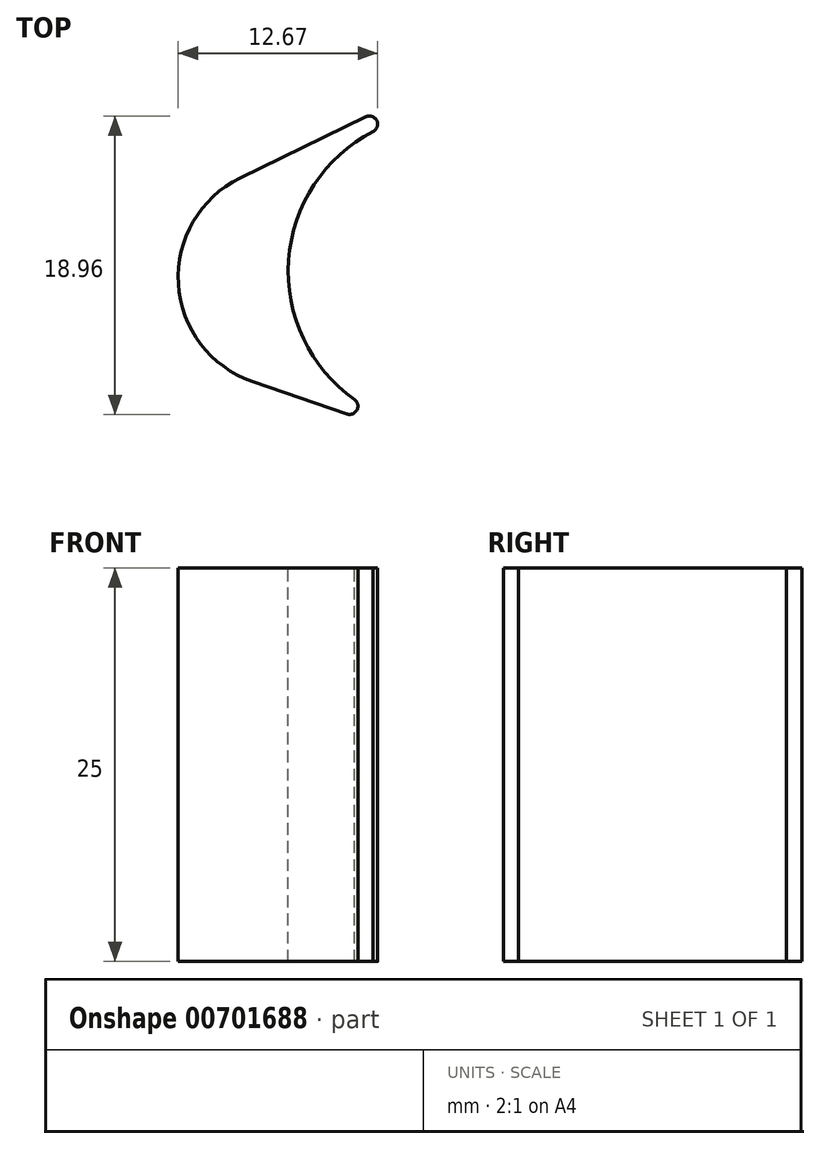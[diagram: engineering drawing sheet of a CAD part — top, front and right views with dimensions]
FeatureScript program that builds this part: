
annotation { "Feature Type Name" : "Feature", "Feature Type Description" : "" }
export const myFeature = defineFeature(function(context is Context, id is Id, definition is map)
    precondition{}
    {
        {
            var Q0;
            Q0=qCreatedBy(makeId("Top.planeOp"),FACE);
            var sketch = newSketch(context, id + "F0", { "sketchPlane" : qUnion([Q0])});
            skArc(sketch, "E0", {"start": v(5.07, 11.42) * mm, "mid": v(-0.3, 3.24) * mm, "end": v(3.88, -5.61) * mm});
            skArc(sketch, "E1", {"start": v(-3.39, 8.45) * mm, "mid": v(-7.3, 1.73) * mm, "end": v(-2.6, -4.46) * mm});
            skLineSegment(sketch, "E2", {"start": v(-3.39, 8.45) * mm, "end": v(4.6, 12.35) * mm});
            skArc(sketch, "E3", {"start": v(5.07, 11.42) * mm, "mid": v(5.3, 12.11) * mm, "end": v(4.6, 12.35) * mm});
            skLineSegment(sketch, "E4", {"start": v(-2.6, -4.46) * mm, "end": v(3.4, -6.53) * mm});
            skArc(sketch, "E5", {"start": v(3.4, -6.53) * mm, "mid": v(4.04, -6.27) * mm, "end": v(3.88, -5.61) * mm});
            skLineSegment(sketch, "E6", {"start": v(5.35, 17.21) * mm, "end": v(5.35, -48.7) * mm, "construction": true});
            skLineSegment(sketch, "E7", {"start": v(6.66, 30.6) * mm, "end": v(2.37, -30.69) * mm, "construction": true});
            skSolve(sketch);
        }
        {
            var Q0;
            Q0=qCreatedBy(makeId("Top.planeOp"),FACE);
            var sketch = newSketch(context, id + "F1", { "sketchPlane" : qUnion([Q0])});
            skLineSegment(sketch, "E8.0", {"start": v(-3.39, 8.45) * mm, "end": v(4.6, 12.35) * mm});
            skArc(sketch, "E9.0", {"start": v(-3.39, 8.45) * mm, "mid": v(-7.3, 1.73) * mm, "end": v(-2.6, -4.46) * mm});
            skLineSegment(sketch, "E10.0", {"start": v(-2.6, -4.46) * mm, "end": v(3.4, -6.53) * mm});
            skArc(sketch, "E11.0", {"start": v(5.07, 11.42) * mm, "mid": v(5.3, 12.11) * mm, "end": v(4.6, 12.35) * mm});
            skArc(sketch, "E12.0", {"start": v(3.4, -6.53) * mm, "mid": v(4.04, -6.27) * mm, "end": v(3.88, -5.61) * mm});
            skSolve(sketch);
        }
        {
            var Q0;
            Q0 = qSketchRegion(id + "F1", true);
            var Q1;
            Q1=sQuery(id+"F1.wireOp",EDGE,"E12.0");
            var Q2;
            Q2=sQuery(id+"F1.wireOp",EDGE,"E10.0");
            var Q3;
            Q3=sQuery(id+"F1.wireOp",EDGE,"E9.0");
            var Q4;
            Q4=sQuery(id+"F1.wireOp",EDGE,"E8.0");
            var Q5;
            Q5=sQuery(id+"F1.wireOp",EDGE,"E11.0");
            extrude(context, id + "F2", {"entities" : qUnion([Q0]), "bodyType" : ToolBodyType.SURFACE, "surfaceEntities" : qUnion([Q1, Q2, Q3, Q4, Q5]), "depth" : 25 * mm, "offsetDistance" : 25 * mm});
        }
        {
            var Q0;
            Q0 = qSketchRegion(id + "F0", true);
            var Q1;
            Q1=sQuery(id+"F0.wireOp",EDGE,"E0");
            extrude(context, id + "F3", {"entities" : qUnion([Q0]), "bodyType" : ToolBodyType.SURFACE, "surfaceEntities" : qUnion([Q1]), "depth" : 25 * mm, "offsetDistance" : 25 * mm});
        }
    });
